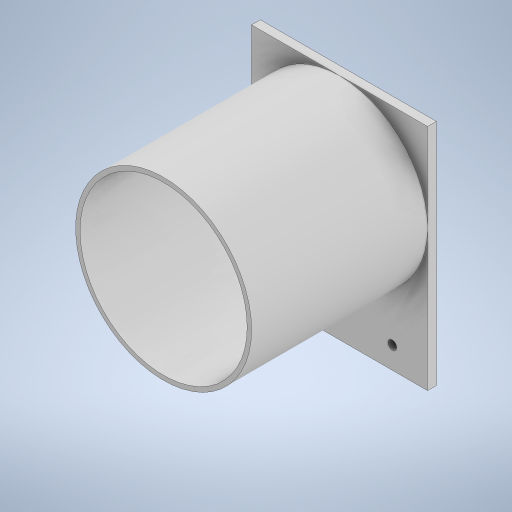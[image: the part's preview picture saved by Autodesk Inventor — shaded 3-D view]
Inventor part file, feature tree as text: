
AUTODESK INVENTOR PART (.ipt)
format: ipt  version: 2024 (Build 280153000, 153)  size: 263,680 bytes
history: native  units: mm
features: extrude x3, sketch x3, thread x2
ambient origin geometry x8: Origin, YZ Plane, XZ Plane, XY Plane, X Axis, Y Axis, Z Axis, Center Point
bodies: Solid1 (feature_tree)
feature tree (8):
  extrude  "Extrusion1"  Depth=130.0mm
  extrude  "Extrusion2"  Depth=5.0mm
  extrude  "Extrusion3"  Depth=5.0mm
  thread  "Thread1"  [1 undecoded]
  thread  "Thread2"  [1 undecoded]
  sketch  "Sketch1"  dims[d0=100.0mm d1=130.0mm]
  sketch  "Sketch2"  dims[d2=5.0mm d3=0.0mm d4=95.0mm]
  sketch  "Sketch3"  dims[d5=100.0mm d6=0.0mm d7=25.0mm d8=5.0mm d9=5.0mm d10=20.0mm d11=20.0mm d12=12.5mm d13=12.5mm d14=100.0mm d15=0.0mm d16=5.0mm d17=0.0mm d18=5.0mm d19=0.0mm]
note: 2 required parameter values undecoded (feature->parameter linkage not recoverable at this tier; creation-order binding heuristic only, values carry confidence <= 0.55)
